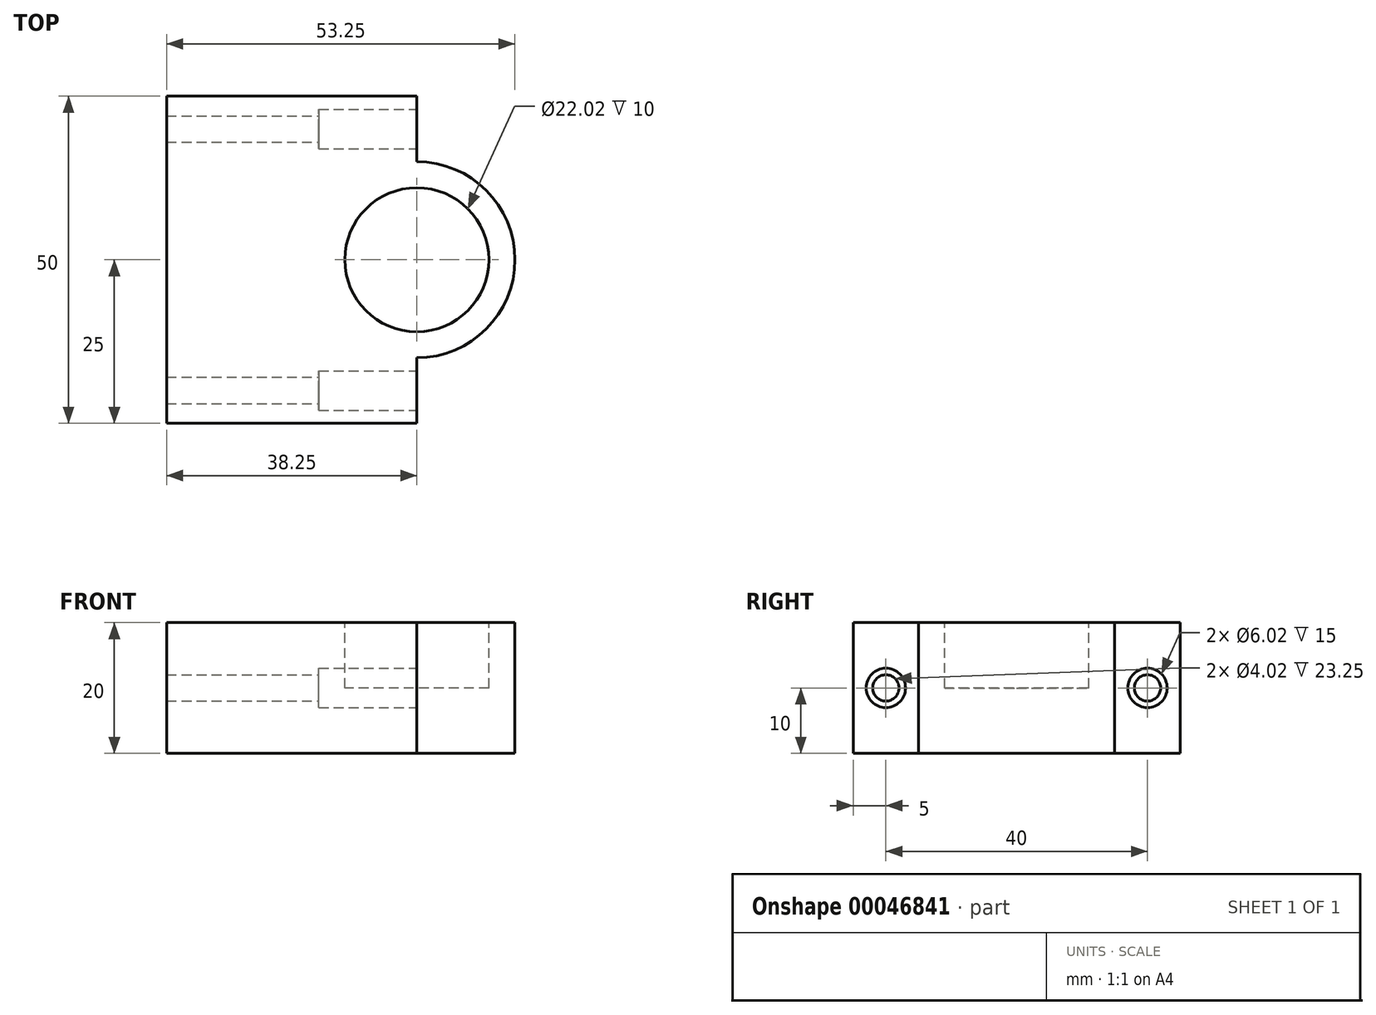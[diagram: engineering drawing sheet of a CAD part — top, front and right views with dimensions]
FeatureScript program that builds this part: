
annotation { "Feature Type Name" : "Feature", "Feature Type Description" : "" }
export const myFeature = defineFeature(function(context is Context, id is Id, definition is map)
    precondition{}
    {
        {
            var Q0;
            Q0=qCreatedBy(makeId("Top.planeOp"),FACE);
            var sketch = newSketch(context, id + "F0", { "sketchPlane" : qUnion([Q0])});
            skLineSegment(sketch, "E0", {"start": v(0, 0) * mm, "end": v(0, 50) * mm});
            skLineSegment(sketch, "E1", {"start": v(0, 50) * mm, "end": v(38.25, 50) * mm});
            skArc(sketch, "E2", {"start": v(38.25, 10) * mm, "mid": v(53.25, 25) * mm, "end": v(38.25, 40) * mm});
            skLineSegment(sketch, "E3", {"start": v(38.25, 25) * mm, "end": v(38.25, 50) * mm, "construction": true});
            skLineSegment(sketch, "E4", {"start": v(0, 0) * mm, "end": v(26.93, 0) * mm});
            skLineSegment(sketch, "E5", {"start": v(26.93, 0) * mm, "end": v(38.25, 0) * mm});
            skLineSegment(sketch, "E6", {"start": v(38.25, 0) * mm, "end": v(38.25, 10) * mm});
            skLineSegment(sketch, "E7", {"start": v(38.25, 50) * mm, "end": v(38.25, 40) * mm});
            skSolve(sketch);
        }
        {
            var Q0;
            Q0=qSketchRegion(id+"F0",true);
            extrude(context, id + "F1", {"entities" : qUnion([Q0]), "depth" : 20 * mm});
        }
        {
            var Q0;
            Q0=makeQuery(id+"F1.opExtrude","CAP_FACE",FACE,{"disambiguationData":[OSD([sQuery(id+"F0.wireOp",EDGE,"E0"),sQuery(id+"F0.wireOp",EDGE,"E1"),sQuery(id+"F0.wireOp",EDGE,"E2"),sQuery(id+"F0.wireOp",EDGE,"E4"),sQuery(id+"F0.wireOp",EDGE,"E5"),sQuery(id+"F0.wireOp",EDGE,"E6"),sQuery(id+"F0.wireOp",EDGE,"E7")])],"isStart":false});
            var sketch = newSketch(context, id + "F2", { "sketchPlane" : qUnion([Q0])});
            skLineSegment(sketch, "E8", {"start": v(38.25, 10) * mm, "end": v(38.25, 40) * mm, "construction": true});
            skCircle(sketch, "E9", {"center": v(38.25, 25) * mm, "radius": 11.01 * mm});
            skSolve(sketch);
        }
        {
            var Q0;
            Q0=qSketchRegion(id+"F2",true);
            extrude(context, id + "F3", {"entities" : qUnion([Q0]), "operationType" : NewBodyOperationType.REMOVE, "oppositeDirection" : true, "depth" : 10 * mm});
        }
        {
            var Q0;
            Q0=makeQuery(id+"F1.opExtrude","SWEPT_FACE",FACE,{"disambiguationData":[OSD([sQuery(id+"F0.wireOp",EDGE,"E7")])]});
            var sketch = newSketch(context, id + "F4", { "sketchPlane" : qUnion([Q0])});
            skLineSegment(sketch, "E10", {"start": v(45, 20) * mm, "end": v(45, 0) * mm, "construction": true});
            skCircle(sketch, "E11", {"center": v(45, 10) * mm, "radius": 3 * mm});
            skSolve(sketch);
        }
        {
            var Q0;
            Q0=qSketchRegion(id+"F4",true);
            extrude(context, id + "F5", {"entities" : qUnion([Q0]), "operationType" : NewBodyOperationType.REMOVE, "oppositeDirection" : true, "depth" : 15 * mm});
        }
        {
            var Q0;
            Q0=makeQuery(id+"F1.opExtrude","SWEPT_FACE",FACE,{"disambiguationData":[OSD([sQuery(id+"F0.wireOp",EDGE,"E6")])]});
            var sketch = newSketch(context, id + "F6", { "sketchPlane" : qUnion([Q0])});
            skLineSegment(sketch, "E12", {"start": v(5, 20) * mm, "end": v(5, 0) * mm, "construction": true});
            skCircle(sketch, "E13", {"center": v(5, 10) * mm, "radius": 3 * mm});
            skSolve(sketch);
        }
        {
            var Q0;
            Q0=qSketchRegion(id+"F6",true);
            extrude(context, id + "F7", {"entities" : qUnion([Q0]), "operationType" : NewBodyOperationType.REMOVE, "oppositeDirection" : true, "depth" : 15 * mm});
        }
        {
            var Q0;
            Q0=makeQuery(id+"F7.boolean.opBoolean","COPY",FACE,{"derivedFrom":makeQuery(id+"F7.opExtrude","CAP_FACE",FACE,{"disambiguationData":[OSD([sQuery(id+"F6.wireOp",EDGE,"E13")])],"isStart":false})});
            var sketch = newSketch(context, id + "F8", { "sketchPlane" : qUnion([Q0])});
            skCircle(sketch, "E14", {"center": v(5, 10) * mm, "radius": 2 * mm});
            skSolve(sketch);
        }
        {
            var Q0;
            Q0=qSketchRegion(id+"F8",true);
            extrude(context, id + "F9", {"entities" : qUnion([Q0]), "operationType" : NewBodyOperationType.REMOVE, "endBound" : BoundingType.THROUGH_ALL, "oppositeDirection" : true, "depth" : 25 * mm});
        }
        {
            var Q0;
            Q0=makeQuery(id+"F5.boolean.opBoolean","COPY",FACE,{"derivedFrom":makeQuery(id+"F5.opExtrude","CAP_FACE",FACE,{"disambiguationData":[OSD([sQuery(id+"F4.wireOp",EDGE,"E11")])],"isStart":false})});
            var sketch = newSketch(context, id + "F10", { "sketchPlane" : qUnion([Q0])});
            skCircle(sketch, "E15", {"center": v(45, 10) * mm, "radius": 2 * mm});
            skSolve(sketch);
        }
        {
            var Q0;
            Q0=qSketchRegion(id+"F10",true);
            extrude(context, id + "F11", {"entities" : qUnion([Q0]), "operationType" : NewBodyOperationType.REMOVE, "endBound" : BoundingType.THROUGH_ALL, "oppositeDirection" : true, "depth" : 25 * mm});
        }
    });
